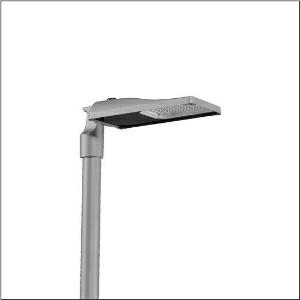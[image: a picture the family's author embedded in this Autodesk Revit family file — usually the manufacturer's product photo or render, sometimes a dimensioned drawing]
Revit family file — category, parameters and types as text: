
# Revit family: streetlight_sl_31_mini___st1_0a_5xh6d31s08ha_c5f6
name_source: partatom
category: Lighting Fixtures
units: mm (PartAtom-declared; Revit-internal decimal feet)

## family parameters
Cut with Voids When Loaded = No
Host = Face
Light Source = No
Part Type = Normal
Room Calculation Point = No
Round Connector Dimension = Use Diameter
Shared = No

## types (1)
- --- (1 x LED, 9230 lm, 68.3 W, 3000K)
    Apparent Load = 68 VA
    CIE Flux Codes = 37 72 97 100 100
    Color Rendering = 70
    Color Temperature = 3000K
    Default Elevation = 1800 mm
    Description = Streetlight SL 31 mini D4i, Desk-Remote mast luminaire for post-top, side-entry; light control with lens of PMMA; light distribution: ST1.0a, direct asymmetric distribution, for standard-compliant lighting for roads and squares; LED: luminous flux: 9.230lm, light colour: 730, colour temperature: 3000K; luminous efficacy: 135,1lm/W; control: pre-setting: logarithmic dimming characteristic, flexible luminous flux parameterisation, time-dependent luminous flux control, constant luminous flux control, power reduction, intelligent temperature release in ECG and LED module, overheat protection; luminaire housing, of diecast aluminium, SITECO metallic grey (DB 702S), corrosivity category C5 high according to DIN EN ISO 12944; cover of toughened safety glass, transparent, opened without tools; mast flange of diecast aluminium, SITECO metallic grey (DB 702S), spigot size: 76/60mm, mast flange included unmounted; with cable H07RN-F 2x 1.5mm², cable length: 8,5m, connection cable pre-assembled; mains connection: 220..240V, AC, 50/60Hz; power consumption (at start of service life): 68,3W / (at end of service life): 74,5W / (with reduced operation 50%): 29,5W; protection rating (complete): IP66; insulation class (complete): insulation class II (safety insulation); impact resistance: IK10; certification: CE, ENEC, ENEC+, VDE, UKCA, ZD4i; permissible operating ambient temperature for outdoor applications: -40..+50°C; packaging unit: 1 piece

Light Distribution: ST1.0a
    Height = 76 mm
    Lamp = 1 x LED
    Lamp Light Flux = 9230 lm
    Lamp Power = 68.3 W
    Lamp count = 1
    Length = 547 mm
    Luminous efficacy = 135 lm/W
    Manufacturer = Siteco
    ModVariant = No
    Model = 5XH6D31S08HA
    Number of Poles = 1
    OnlyDefault = Yes
    Power Factor = 1
    Product Name = Streetlight SL 31 mini | ST1.0a
    Product group = mast luminaire | pylon top
    ProductGroupID = 6100
    Protection Class = Protection class II
    Protection Degree = IP 66
    RLX_Detail_Level = 1
    RLX_Emergency_Light_Flux = 0 lm
    RLX_Emergency_Type = 0
    RLX_Emergency_Type_DB = No
    RlxData = <blob elided: 24173 chars, md5=ec8269f8>
    Socket = socket
    Standby Power = 0 W
    System Light Flux = 9230 lm
    System Power = 68 W
    Type Comments = factory setting: luminous flux: 100 % | dim-lin: 254 | 692 mA
    Type Image = l_1300330.jpg
    URL = http://relux.com
    VarID = @adj_020359
    Voltage = 0 V
    Weight = 0.00 kg
    Width = 265 mm

## geometry (parser evidence)
native form markers: Blend x4, Sweep x10
no freeform markers — native parametric forms only
